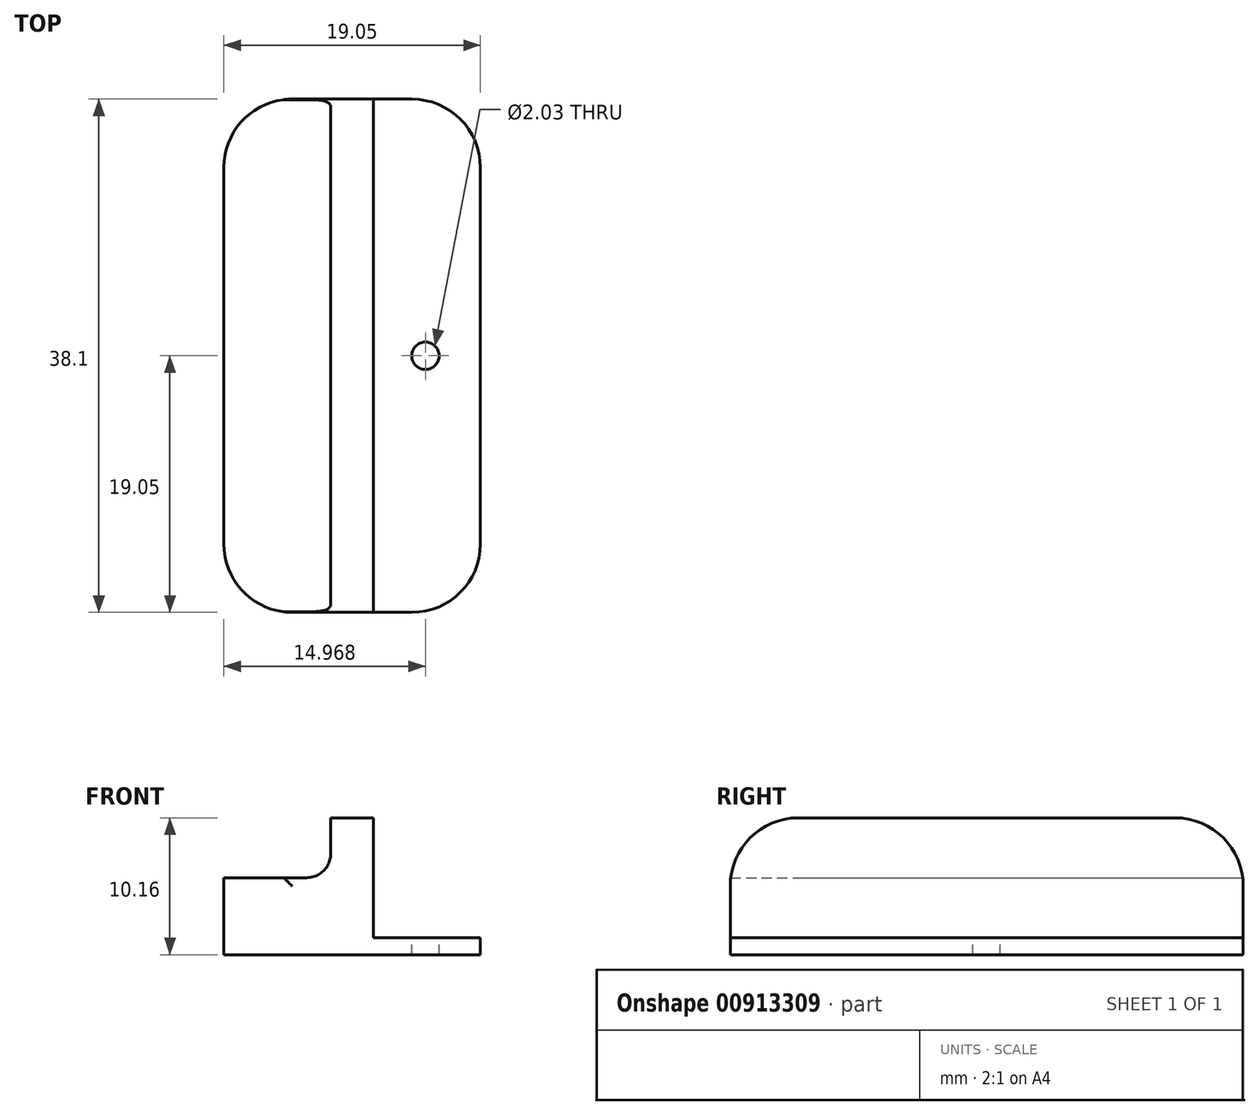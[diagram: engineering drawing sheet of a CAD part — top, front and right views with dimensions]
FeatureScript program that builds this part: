
annotation { "Feature Type Name" : "Feature", "Feature Type Description" : "" }
export const myFeature = defineFeature(function(context is Context, id is Id, definition is map)
    precondition{}
    {
        {
            var Q0;
            Q0=qCreatedBy(makeId("Front.planeOp"),FACE);
            var sketch = newSketch(context, id + "F0", { "sketchPlane" : qUnion([Q0])});
            skLineSegment(sketch, "E0", {"start": v(0, 0) * mm, "end": v(19.05, 0) * mm});
            skLineSegment(sketch, "E1", {"start": v(19.05, 0) * mm, "end": v(19.05, 1.27) * mm});
            skLineSegment(sketch, "E2", {"start": v(19.05, 1.27) * mm, "end": v(11.11, 1.27) * mm});
            skLineSegment(sketch, "E3", {"start": v(11.11, 1.27) * mm, "end": v(11.11, 10.16) * mm});
            skLineSegment(sketch, "E4", {"start": v(11.11, 10.16) * mm, "end": v(7.94, 10.16) * mm});
            skLineSegment(sketch, "E5", {"start": v(7.94, 10.16) * mm, "end": v(7.94, 5.72) * mm});
            skLineSegment(sketch, "E6", {"start": v(7.94, 5.72) * mm, "end": v(0, 5.72) * mm});
            skLineSegment(sketch, "E7", {"start": v(0, 5.72) * mm, "end": v(0, 0) * mm});
            skSolve(sketch);
        }
        {
            var Q0;
            Q0=makeQuery(id+"F0.imprint","IMPRINT",FACE,{"disambiguationData":[TD([[makeQuery(id+"F0.imprint","IMPRINT",EDGE,{"derivedFrom":sQuery(id+"F0.wireOp",EDGE,"E0")}),1.0]])]});
            extrude(context, id + "F1", {"entities" : qUnion([Q0]), "depth" : 38.1 * mm, "offsetDistance" : 25.4 * mm});
        }
        {
            var Q0;
            Q0=makeQuery(id+"F1.opExtrude","SWEPT_EDGE",EDGE,{"disambiguationData":[OSD([sQuery(id+"F0.wireOp",EDGE,"E5"),sQuery(id+"F0.wireOp",EDGE,"E6")])]});
            fillet(context, id + "F2", {"entities" : qUnion([Q0]), "radius" : 1.78 * mm, "tangentPropagation" : true, "allowEdgeOverflow" : false});
        }
        {
            var Q0;
            Q0=makeQuery(id+"F1.opExtrude","CAP_EDGE",EDGE,{"disambiguationData":[OSD([sQuery(id+"F0.wireOp",EDGE,"E1")])],"isStart":false});
            var Q1;
            Q1=makeQuery(id+"F1.opExtrude","CAP_EDGE",EDGE,{"disambiguationData":[OSD([sQuery(id+"F0.wireOp",EDGE,"E7")])],"isStart":false});
            var Q2;
            Q2=makeQuery(id+"F1.opExtrude","CAP_EDGE",EDGE,{"disambiguationData":[OSD([sQuery(id+"F0.wireOp",EDGE,"E7")])],"isStart":true});
            var Q3;
            Q3=makeQuery(id+"F1.opExtrude","CAP_EDGE",EDGE,{"disambiguationData":[OSD([sQuery(id+"F0.wireOp",EDGE,"E1")])],"isStart":true});
            fillet(context, id + "F3", {"entities" : qUnion([Q0, Q1, Q2, Q3]), "radius" : 5.08 * mm, "tangentPropagation" : true, "allowEdgeOverflow" : false});
        }
        {
            var Q0;
            Q0=makeQuery(id+"F1.opExtrude","SWEPT_FACE",FACE,{"disambiguationData":[OSD([sQuery(id+"F0.wireOp",EDGE,"E2")])]});
            var sketch = newSketch(context, id + "F4", { "sketchPlane" : qUnion([Q0])});
            skLineSegment(sketch, "E8", {"start": v(19.05, -19.05) * mm, "end": v(-5.04, -19.05) * mm, "construction": true});
            skCircle(sketch, "E9", {"center": v(14.97, -19.05) * mm, "radius": 1.02 * mm});
            skSolve(sketch);
        }
        {
            var Q0;
            Q0 = qSketchRegion(id + "F4", true);
            extrude(context, id + "F5", {"entities" : qUnion([Q0]), "operationType" : NewBodyOperationType.REMOVE, "oppositeDirection" : true, "depth" : 25.4 * mm, "offsetDistance" : 25.4 * mm});
        }
        {
            var Q0;
            Q0=makeQuery(id+"F1.opExtrude","CAP_EDGE",EDGE,{"disambiguationData":[OSD([sQuery(id+"F0.wireOp",EDGE,"E4")])],"isStart":false});
            var Q1;
            Q1=makeQuery(id+"F1.opExtrude","CAP_EDGE",EDGE,{"disambiguationData":[OSD([sQuery(id+"F0.wireOp",EDGE,"E4")])],"isStart":true});
            fillet(context, id + "F6", {"entities" : qUnion([Q0, Q1]), "radius" : 5.08 * mm, "tangentPropagation" : true, "allowEdgeOverflow" : false});
        }
    });
